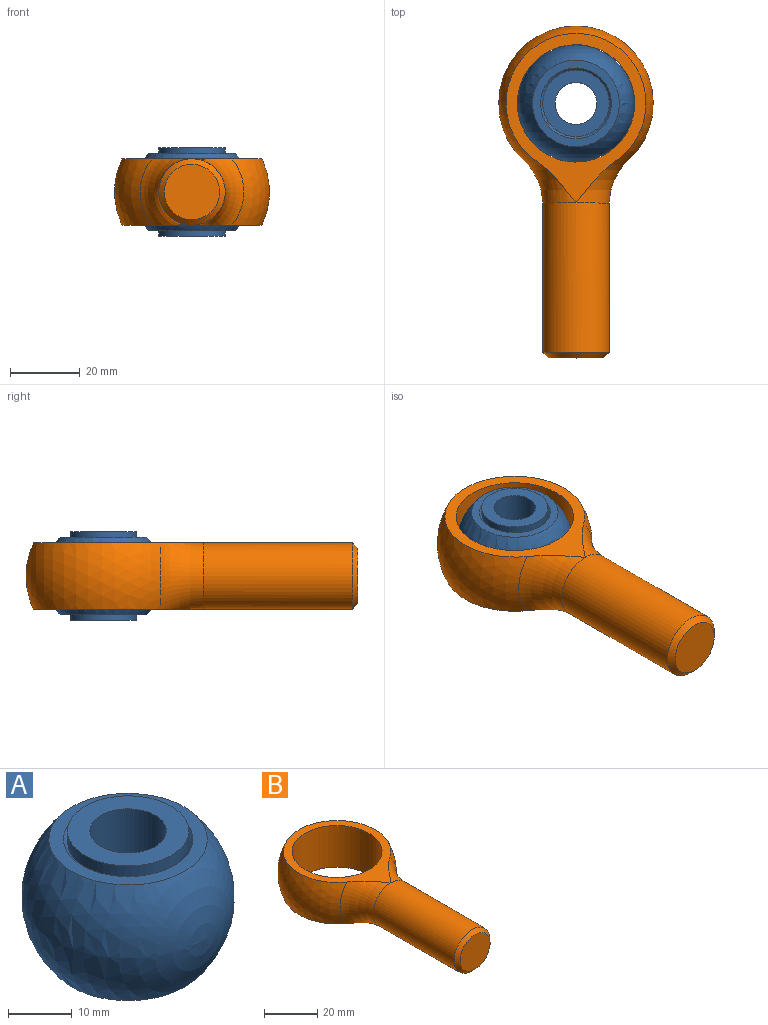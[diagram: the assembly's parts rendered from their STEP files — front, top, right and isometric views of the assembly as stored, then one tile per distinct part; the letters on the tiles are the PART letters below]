
ASSEMBLY  parts=2 mates=1
PART A: 10 faces, bbox 33.4x33.4x33.4 mm
  f0: sphere r=16.68mm, area 2328.6mm2, adj f1,f2
  f1: plane 24.87x24.87mm, normal (0,0,1), area 161.3mm2, adj f0,f3
  f2: plane 24.87x24.87mm, normal (0,0,-1), area 161.3mm2, adj f0,f4
  f3: cone r=9.53mm half-angle=45deg, axis (0,0,1), area 55.5mm2, adj f1,f7
  f4: cone r=10.16mm half-angle=45deg, axis (0,0,-1), area 55.5mm2, adj f2,f6
  f5: plane 19.05x19.05mm, normal (0,0,-1), area 171.9mm2, adj f6,f9
  f6: cylinder r=9.53mm len=19.05mm, axis (0,0,-1), area 133mm2, adj f4,f5
  f7: cylinder r=9.53mm len=19.05mm, axis (0,0,-1), area 133mm2, adj f3,f8
  f8: plane 19.05x19.05mm, normal (0,0,1), area 171.9mm2, adj f7,f9
  f9: cylinder r=6mm len=25.4mm, axis (0,0,1), area 957.6mm2, adj f5,f8
PART B: 9 faces, bbox 55.8x95.3x55.8 mm
  f0: torus R=25.8mm, axis (0,-1,0), area 324.5mm2, adj f2,f5,f6,f7
  f1: plane 15.88x15.88mm, normal (0,-1,0), area 197.9mm2, adj f3
  f2: cylinder r=9.53mm len=42.86mm, axis (0,1,0), area 2565.2mm2, adj f0,f3,f4
  f3: cone r=9.53mm half-angle=45deg, axis (0,1,0), area 123.2mm2, adj f1,f2
  f4: torus R=25.8mm, axis (0,-1,0), area 324.5mm2, adj f2,f5,f6,f7
  f5: sphere r=22.23mm, area 2071.2mm2, adj f0,f4,f6,f7
  f6: plane 48.66x40.16mm, normal (0,0,1), area 444.3mm2, adj f0,f4,f5,f8
  f7: plane 48.66x40.16mm, normal (0,0,-1), area 444.3mm2, adj f0,f4,f5,f8
  f8: cylinder r=16.84mm len=33.67mm, axis (0,0,1), area 2015.1mm2, adj f6,f7
PLACE A t=(0,28.58,0)mm
PLACE B at identity
MATE ball A.f3 <-> B.f8  axis (0,0,1) through (0,28.58,0)mm
